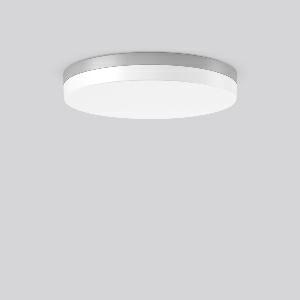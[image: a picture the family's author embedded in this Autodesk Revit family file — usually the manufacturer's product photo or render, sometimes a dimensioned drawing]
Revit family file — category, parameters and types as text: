
# Revit family: flat_slim_round_312633_004_19_ef8f
name_source: partatom
category: Lighting Fixtures
units: mm (PartAtom-declared; Revit-internal decimal feet)

## family parameters
Cut with Voids When Loaded = No
Host = Face
Light Source = No
Part Type = Normal
Room Calculation Point = No
Round Connector Dimension = Use Diameter
Shared = No

## types (1)
- MultiLumen 1 830 (1 x LED Modul 830, 3350 lm, 3000)
    Apparent Load = 31 VA
    CIE Flux Codes = 41 71 90 86 100
    Color Rendering = 80
    Color Temperature = 3000
    Default Elevation = 1800 mm
    Height = 75 mm
    Lamp = 1 x LED Modul 830
    Lamp Light Flux = 3350 lm
    Lamp count = 1
    Length = 480 mm
    Lifetime = 50000 h
    Luminous efficacy = 108 lm/W
    Manufacturer = RZB
    ModVariant = No
    Model = 312633.004.19
    Mounting Place = Ceiling
    Mounting Type = Surface mounted
    Number of Poles = 1
    OnlyDefault = Yes
    Power Factor = 1
    Product Name = FLAT SLIM round
    Product group = Surface mounted ceiling and wall luminaires
    ProductGroupID = 305
    Protection Class = Protection class I
    Protection Degree = Degree of protection
    RLX_Detail_Level = 1
    RLX_Emergency_Light_Flux = 0 lm
    RLX_Emergency_Type = 0
    RLX_Emergency_Type_DB = No
    RlxData = <blob elided: 22269 chars, md5=7ba07287>
    Socket = socket
    Standby Power = 0 W
    System Light Flux = 3350 lm
    System Power = 31 W
    Type Comments = MultiLumen 1 830
    Type Image = 312633.004.jpg
    URL = http://relux.com
    VarID = multilumen_1_830
    Voltage = 0 V
    Weight = 0.00 kg
    Width = 0 mm  [stored 0 ft]

note: [stored X ft] marks values corroborated as IEEE doubles in the binary element streams (Revit-internal decimal feet)

## geometry (parser evidence)
native form markers: Blend x4, Sweep x13
no freeform markers — native parametric forms only
